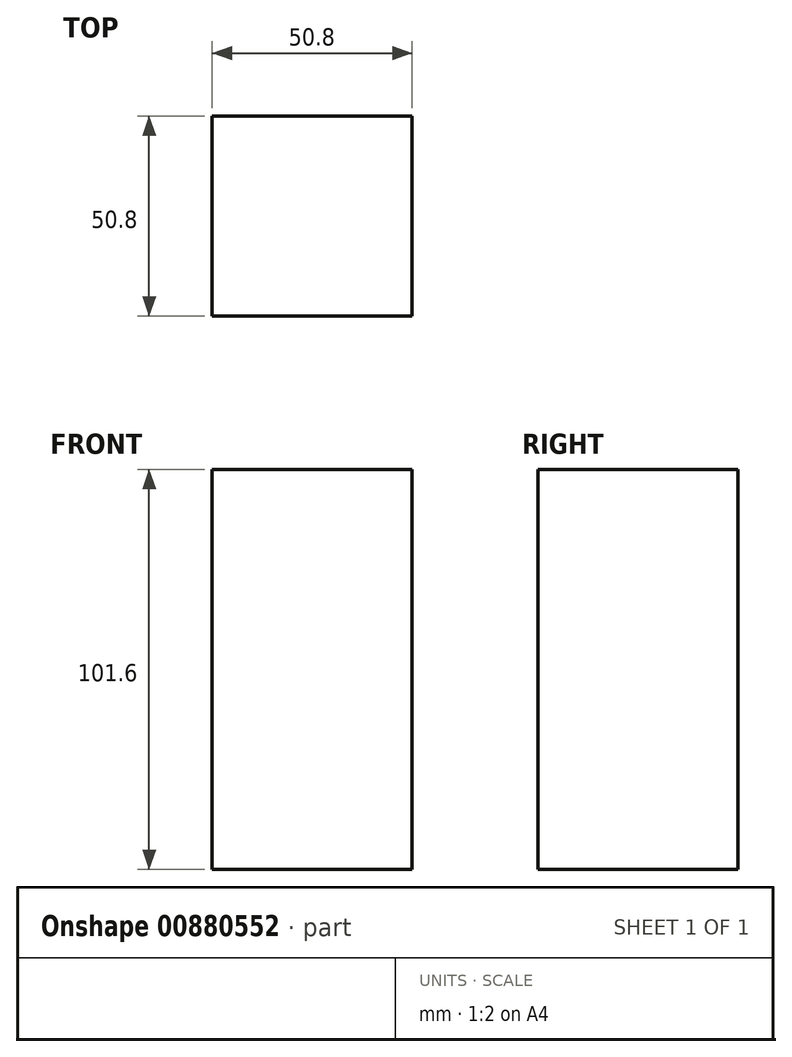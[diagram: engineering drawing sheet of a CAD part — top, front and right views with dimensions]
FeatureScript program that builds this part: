
annotation { "Feature Type Name" : "Feature", "Feature Type Description" : "" }
export const myFeature = defineFeature(function(context is Context, id is Id, definition is map)
    precondition{}
    {
        {
            var Q0;
            Q0=qCreatedBy(makeId("Front.planeOp"),FACE);
            var sketch = newSketch(context, id + "F0", { "sketchPlane" : qUnion([Q0])});
            skLineSegment(sketch, "E0.bottom", {"start": v(0, 0) * mm, "end": v(50.8, 0) * mm});
            skLineSegment(sketch, "E0.top", {"start": v(0, 101.6) * mm, "end": v(50.8, 101.6) * mm});
            skLineSegment(sketch, "E0.left", {"start": v(0, 0) * mm, "end": v(0, 101.6) * mm});
            skLineSegment(sketch, "E0.right", {"start": v(50.8, 0) * mm, "end": v(50.8, 101.6) * mm});
            skSolve(sketch);
        }
        {
            var Q0;
            Q0=makeQuery(id+"F0.imprint","IMPRINT",FACE,{"disambiguationData":[TD([[makeQuery(id+"F0.imprint","IMPRINT",EDGE,{"derivedFrom":sQuery(id+"F0.wireOp",EDGE,"E0.bottom")}),1.0]])]});
            extrude(context, id + "F1", {"entities" : qUnion([Q0]), "oppositeDirection" : true, "depth" : 50.8 * mm, "offsetDistance" : 25.4 * mm});
        }
    });
